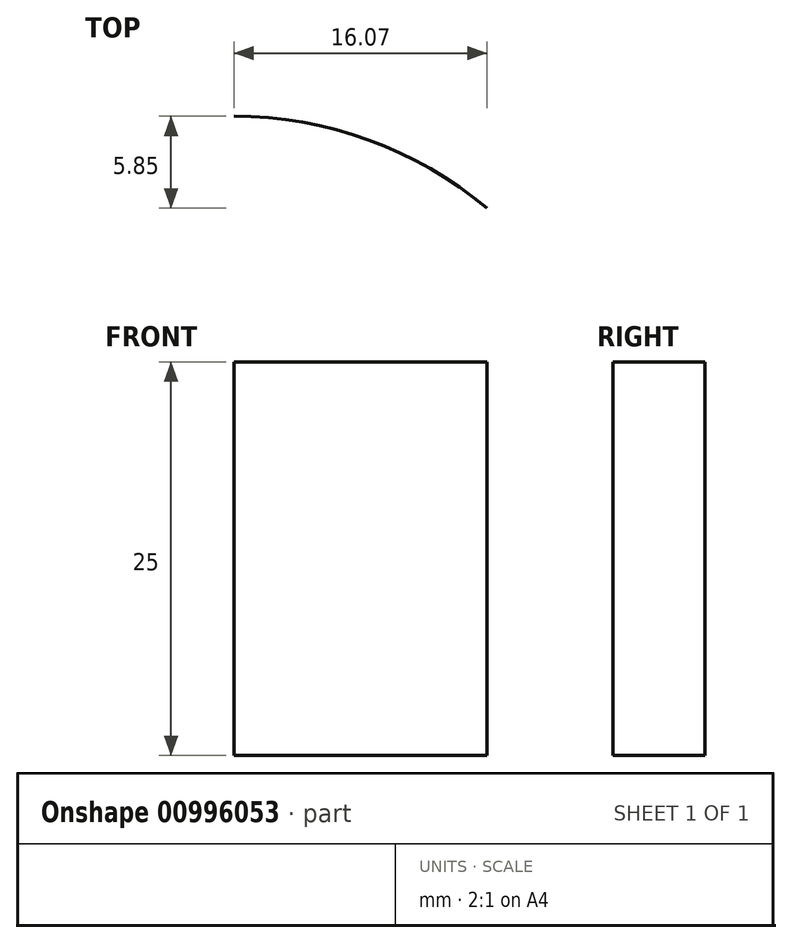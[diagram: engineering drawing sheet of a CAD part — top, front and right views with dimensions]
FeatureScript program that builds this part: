
annotation { "Feature Type Name" : "Feature", "Feature Type Description" : "" }
export const myFeature = defineFeature(function(context is Context, id is Id, definition is map)
    precondition{}
    {
        {
            var Q0;
            Q0=qCreatedBy(makeId("Top.planeOp"),FACE);
            var sketch = newSketch(context, id + "F0", { "sketchPlane" : qUnion([Q0])});
            skArc(sketch, "E0", {"start": v(0, 0) * mm, "mid": v(8.55, -1.5) * mm, "end": v(16.07, -5.85) * mm});
            skLineSegment(sketch, "E1", {"start": v(0, -25) * mm, "end": v(17.67, -3.95) * mm, "construction": true});
            skSolve(sketch);
        }
        {
            var Q0;
            Q0=sQuery(id+"F0.wireOp",EDGE,"E0");
            extrude(context, id + "F1", {"bodyType" : ToolBodyType.SURFACE, "surfaceEntities" : qUnion([Q0]), "oppositeDirection" : true, "depth" : 25 * mm, "offsetDistance" : 25 * mm});
        }
    });
